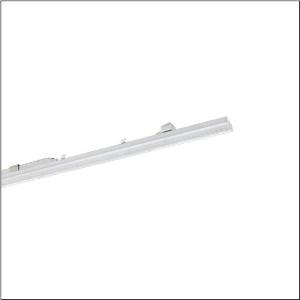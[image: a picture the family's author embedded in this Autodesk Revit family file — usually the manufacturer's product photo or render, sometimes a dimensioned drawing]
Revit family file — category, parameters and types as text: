
# Revit family: tl_l_5wd7a8f0h2b5
name_source: partatom
category: Lighting Fixtures
units: mm (PartAtom-declared; Revit-internal decimal feet)

## family parameters
Cut with Voids When Loaded = No
Host = Face
Light Source = No
Part Type = Normal
Room Calculation Point = No
Round Connector Dimension = Use Diameter
Shared = No

## types (1)
- TL L (1 x LED, 4990 lm, 30 W, 4000K)
    Apparent Load = 30 VA
    CIE Flux Codes = 49 84 98 100 100
    Color Rendering = 80
    Color Temperature = 4000K
    Default Elevation = 1800 mm
    Description = TL L, luminaire insert, of sheet steel, galvanised, coil coated, white, length: 1.500mm, width: 66mm, height: 67mm, surge protection,LED rated luminous flux: 4.990lm, light colour: 840, control gear: 4..20mA, with terminal, 5-pole, mains connection: 230..240V, AC, 50/60Hz, rated input power: 30W, micro fuse,primary optical cover: cover, of PMMA, light emission: direct distribution, protection rating (complete): as luminaire, insulation class (complete): insulation class I (protective earthing), certification: CE, impact resistance: IK06, permissible ambient temperature for indoor applications: -25..+35°C, packaging unit: 1 piece
    Height = 120 mm
    Lamp = 1 x LED
    Lamp Light Flux = 4990 lm
    Lamp Power = 30 W
    Lamp count = 1
    Length = 1690 mm
    Luminous efficacy = 166 lm/W
    Manufacturer = Siteco
    ModVariant = No
    Model = 5WD7A8F0H2B5
    Mounting Place = Ceiling
    Mounting Type = Pendant
    Number of Poles = 1
    OnlyDefault = Yes
    Power Factor = 1
    Product Name = TL L
    Product group = luminaire insert
    ProductGroupID = 901
    Protection Class = Protection class I
    Protection Degree = Degree of protection
    RLX_Detail_Level = 1
    RLX_Emergency_Light_Flux = 0 lm
    RLX_Emergency_Type = 0
    RLX_Emergency_Type_DB = No
    RlxData = <blob elided: 14129 chars, md5=2f004268>
    Socket = socket
    Standby Power = 0 W
    System Light Flux = 4990 lm
    System Power = 30 W
    Type Comments = Product without accessories
    Type Image = l_1294382.jpg
    URL = http://relux.com
    VarID = ---
    Voltage = 0 V
    Weight = 0.00 kg
    Width = 208 mm

## geometry (parser evidence)
native form markers: Sweep x10
no freeform markers — native parametric forms only
